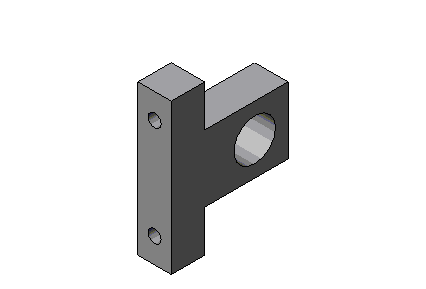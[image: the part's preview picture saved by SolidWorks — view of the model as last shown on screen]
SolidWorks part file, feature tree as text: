
SOLIDWORKS PART (.sldprt)
format: sldprt  version: not decoded by parser v0  size: 99,328 bytes
history: native  units: mm
features: sketch x5, cut_extrude x2, extrude x1, hole x1 (+10 scaffold rows collapsed)
feature tree (19):
  scaffold x10  (default folders/planes/origin — collapsed)
  sketch  "Sketch1"  dims[D1=44.45mm D2=57.15mm]
  extrude  "Extrude1"  Depth=12.7mm
  sketch  "Sketch2"  dims[c1.D1=~10.435107mm c1.D2=15.875mm c2.D1=31.75mm]
  cut_extrude  "Cut-Extrude1"  [1 undecoded]
  sketch  "Sketch3"  dims[c1.D2=38.1mm c1.D3=38.1mm c1.D4=15.875mm c1.D5=12.7mm c2.D2=12.7mm c2.D3=15.875mm c2.D1=0.0mm]
  cut_extrude  "Cut-Extrude2"  [1 undecoded]
  hole  "CBORE for #10 Binding Head Machine Screw1"  Diameter=4.9784mm Depth=12.7mm
  sketch  "Sketch5"  dims[D1=38.1mm]
  sketch  "Sketch4"  dims[hole-wizard template sketch: 42 standard entries collapsed; hole parameters kept: c12.Thru Hole Depth=12.7mm c12.C'Bore Dia.=11.1125mm c12.C'Bore Depth=3.1242mm]
decode coverage: 7 of 9 modeling features carry decoded parameters
note: ~ marks probable driven/reference dimensions
note: 2 parameter values undecoded
note: suppression state not decoded; provenance and decode notes live in map.json
